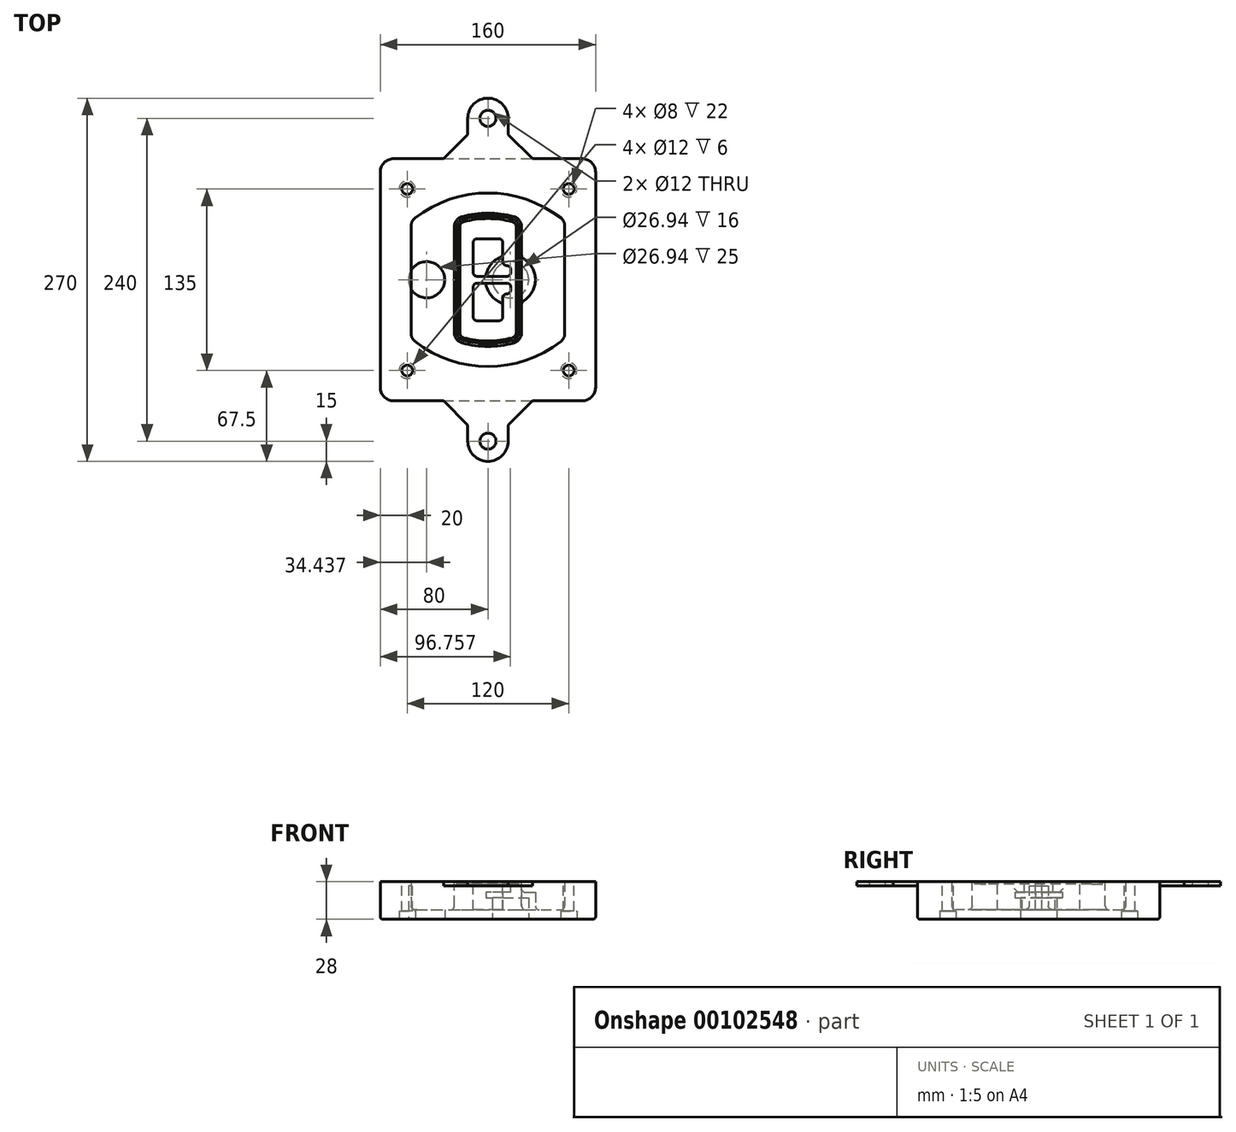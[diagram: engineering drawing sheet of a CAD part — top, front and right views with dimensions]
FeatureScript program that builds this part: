
annotation { "Feature Type Name" : "Feature", "Feature Type Description" : "" }
export const myFeature = defineFeature(function(context is Context, id is Id, definition is map)
    precondition{}
    {
        {
            var Q0;
            Q0=qCreatedBy(makeId("Top.planeOp"),FACE);
            var sketch = newSketch(context, id + "F0", { "sketchPlane" : qUnion([Q0])});
            skPoint(sketch, "E0.rect.middle", {"position": v(0, 0) * mm});
            skLineSegment(sketch, "E1.bottom", {"start": v(-70, -90) * mm, "end": v(70, -90) * mm});
            skLineSegment(sketch, "E1.top", {"start": v(-70, 90) * mm, "end": v(70, 90) * mm});
            skLineSegment(sketch, "E1.left", {"start": v(-80, -80) * mm, "end": v(-80, 80) * mm});
            skLineSegment(sketch, "E1.right", {"start": v(80, -80) * mm, "end": v(80, 80) * mm});
            skLineSegment(sketch, "E2", {"start": v(-80, 90) * mm, "end": v(80, -90) * mm, "construction": true});
            skLineSegment(sketch, "E3", {"start": v(80, 90) * mm, "end": v(-80, -90) * mm, "construction": true});
            skCircle(sketch, "E4", {"center": v(-60, 67.5) * mm, "radius": 4 * mm});
            skCircle(sketch, "E5", {"center": v(60, 67.5) * mm, "radius": 4 * mm});
            skCircle(sketch, "E6", {"center": v(60, -67.5) * mm, "radius": 4 * mm});
            skCircle(sketch, "E7", {"center": v(-60, -67.5) * mm, "radius": 4 * mm});
            skLineSegment(sketch, "E8", {"start": v(-60, 67.5) * mm, "end": v(60, 67.5) * mm, "construction": true});
            skLineSegment(sketch, "E9", {"start": v(60, 67.5) * mm, "end": v(60, -67.5) * mm, "construction": true});
            skLineSegment(sketch, "E10", {"start": v(60, -67.5) * mm, "end": v(-60, -67.5) * mm, "construction": true});
            skLineSegment(sketch, "E11", {"start": v(-60, -67.5) * mm, "end": v(-60, 67.5) * mm, "construction": true});
            skLineSegment(sketch, "E12", {"start": v(-60, 40.3) * mm, "end": v(-60, -40.3) * mm});
            skLineSegment(sketch, "E13", {"start": v(60, 40.3) * mm, "end": v(60, -40.3) * mm});
            skArc(sketch, "E14", {"start": v(56.15, 48.18) * mm, "mid": v(0, 67.5) * mm, "end": v(-56.15, 48.18) * mm});
            skArc(sketch, "E15", {"start": v(-56.15, -48.18) * mm, "mid": v(0, -67.5) * mm, "end": v(56.15, -48.18) * mm});
            skLineSegment(sketch, "E16", {"start": v(-60, 0) * mm, "end": v(60, 0) * mm, "construction": true});
            skPoint(sketch, "E17.visualSharp", {"position": v(-60, -45) * mm});
            skArc(sketch, "E17.filletArc", {"start": v(-60, -40.3) * mm, "mid": v(-58.99, -44.68) * mm, "end": v(-56.15, -48.18) * mm});
            skPoint(sketch, "E18.visualSharp", {"position": v(-60, 45) * mm});
            skArc(sketch, "E18.filletArc", {"start": v(-56.15, 48.18) * mm, "mid": v(-58.99, 44.68) * mm, "end": v(-60, 40.3) * mm});
            skPoint(sketch, "E19.visualSharp", {"position": v(60, 45) * mm});
            skArc(sketch, "E19.filletArc", {"start": v(60, 40.3) * mm, "mid": v(58.99, 44.68) * mm, "end": v(56.15, 48.18) * mm});
            skPoint(sketch, "E20.visualSharp", {"position": v(60, -45) * mm});
            skArc(sketch, "E20.filletArc", {"start": v(56.15, -48.18) * mm, "mid": v(58.99, -44.68) * mm, "end": v(60, -40.3) * mm});
            skPoint(sketch, "E21.visualSharp", {"position": v(-80, 90) * mm});
            skArc(sketch, "E21.filletArc", {"start": v(-70, 90) * mm, "mid": v(-77.07, 87.07) * mm, "end": v(-80, 80) * mm});
            skPoint(sketch, "E22.visualSharp", {"position": v(80, 90) * mm});
            skArc(sketch, "E22.filletArc", {"start": v(80, 80) * mm, "mid": v(77.07, 87.07) * mm, "end": v(70, 90) * mm});
            skPoint(sketch, "E23.visualSharp", {"position": v(80, -90) * mm});
            skArc(sketch, "E23.filletArc", {"start": v(70, -90) * mm, "mid": v(77.07, -87.07) * mm, "end": v(80, -80) * mm});
            skPoint(sketch, "E24.visualSharp", {"position": v(-80, -90) * mm});
            skArc(sketch, "E24.filletArc", {"start": v(-80, -80) * mm, "mid": v(-77.07, -87.07) * mm, "end": v(-70, -90) * mm});
            skArc(sketch, "E25.0", {"start": v(57, 40.3) * mm, "mid": v(56.3, 43.36) * mm, "end": v(54.3, 45.81) * mm});
            skLineSegment(sketch, "E25.1", {"start": v(57, 40.3) * mm, "end": v(57, -40.3) * mm});
            skArc(sketch, "E25.2", {"start": v(54.3, -45.81) * mm, "mid": v(56.3, -43.36) * mm, "end": v(57, -40.3) * mm});
            skArc(sketch, "E25.3", {"start": v(-54.3, -45.81) * mm, "mid": v(0, -64.5) * mm, "end": v(54.3, -45.81) * mm});
            skArc(sketch, "E25.4", {"start": v(-57, -40.3) * mm, "mid": v(-56.3, -43.36) * mm, "end": v(-54.3, -45.81) * mm});
            skArc(sketch, "E25.5", {"start": v(54.3, 45.81) * mm, "mid": v(0, 64.5) * mm, "end": v(-54.3, 45.81) * mm});
            skLineSegment(sketch, "E25.6", {"start": v(-57, 40.3) * mm, "end": v(-57, -40.3) * mm});
            skArc(sketch, "E25.7", {"start": v(-54.3, 45.81) * mm, "mid": v(-56.3, 43.36) * mm, "end": v(-57, 40.3) * mm});
            skArc(sketch, "E26.0", {"start": v(-58.62, 51.33) * mm, "mid": v(-62.58, 46.43) * mm, "end": v(-64, 40.3) * mm});
            skArc(sketch, "E26.1", {"start": v(58.62, 51.33) * mm, "mid": v(0, 71.5) * mm, "end": v(-58.62, 51.33) * mm});
            skArc(sketch, "E26.2", {"start": v(64, 40.3) * mm, "mid": v(62.58, 46.43) * mm, "end": v(58.62, 51.33) * mm});
            skLineSegment(sketch, "E26.3", {"start": v(64, 40.3) * mm, "end": v(64, -40.3) * mm});
            skArc(sketch, "E26.4", {"start": v(58.62, -51.33) * mm, "mid": v(62.58, -46.43) * mm, "end": v(64, -40.3) * mm});
            skLineSegment(sketch, "E26.5", {"start": v(-64, 40.3) * mm, "end": v(-64, -40.3) * mm});
            skArc(sketch, "E26.6", {"start": v(-58.62, -51.33) * mm, "mid": v(0, -71.5) * mm, "end": v(58.62, -51.33) * mm});
            skArc(sketch, "E26.7", {"start": v(-64, -40.3) * mm, "mid": v(-62.58, -46.43) * mm, "end": v(-58.62, -51.33) * mm});
            skSolve(sketch);
        }
        {
            var Q0;
            Q0=makeQuery(id+"F0.imprint","IMPRINT",FACE,{"disambiguationData":[TD([[makeQuery(id+"F0.imprint","IMPRINT",EDGE,{"derivedFrom":sQuery(id+"F0.wireOp",EDGE,"E1.bottom")}),1.0]])]});
            var Q1;
            Q1=makeQuery(id+"F0.imprint","IMPRINT",FACE,{"disambiguationData":[TD([[makeQuery(id+"F0.imprint","IMPRINT",EDGE,{"derivedFrom":sQuery(id+"F0.wireOp",EDGE,"E12")}),1.0]])]});
            var Q2;
            Q2=makeQuery(id+"F0.imprint","IMPRINT",FACE,{"disambiguationData":[TD([[makeQuery(id+"F0.imprint","IMPRINT",EDGE,{"derivedFrom":sQuery(id+"F0.wireOp",EDGE,"E25.0")}),1.0]])]});
            var Q3;
            Q3=makeQuery(id+"F0.imprint","IMPRINT",FACE,{"disambiguationData":[TD([[makeQuery(id+"F0.imprint","IMPRINT",EDGE,{"derivedFrom":sQuery(id+"F0.wireOp",EDGE,"E12")}),-1.0]])]});
            extrude(context, id + "F1", {"entities" : qUnion([Q0, Q1, Q2, Q3]), "oppositeDirection" : true, "depth" : 25 * mm});
        }
        {
            var Q0;
            Q0=makeQuery(id+"F0.imprint","IMPRINT",FACE,{"disambiguationData":[TD([[makeQuery(id+"F0.imprint","IMPRINT",EDGE,{"derivedFrom":sQuery(id+"F0.wireOp",EDGE,"E12")}),1.0]])]});
            extrude(context, id + "F2", {"entities" : qUnion([Q0]), "operationType" : NewBodyOperationType.ADD, "depth" : 3 * mm});
        }
        {
            var Q0;
            Q0=makeQuery(id+"F0.imprint","IMPRINT",FACE,{"disambiguationData":[TD([[makeQuery(id+"F0.imprint","IMPRINT",EDGE,{"derivedFrom":sQuery(id+"F0.wireOp",EDGE,"E25.0")}),1.0]])]});
            extrude(context, id + "F3", {"entities" : qUnion([Q0]), "operationType" : NewBodyOperationType.REMOVE, "oppositeDirection" : true, "depth" : 18 * mm});
        }
        {
            var Q0;
            Q0=makeQuery(id+"F2.opExtrude","CAP_FACE",FACE,{"disambiguationData":[OSD([sQuery(id+"F0.wireOp",EDGE,"E12"),sQuery(id+"F0.wireOp",EDGE,"E13"),sQuery(id+"F0.wireOp",EDGE,"E14"),sQuery(id+"F0.wireOp",EDGE,"E15"),sQuery(id+"F0.wireOp",EDGE,"E17.filletArc"),sQuery(id+"F0.wireOp",EDGE,"E18.filletArc"),sQuery(id+"F0.wireOp",EDGE,"E19.filletArc"),sQuery(id+"F0.wireOp",EDGE,"E20.filletArc"),sQuery(id+"F0.wireOp",EDGE,"E25.0"),sQuery(id+"F0.wireOp",EDGE,"E25.1"),sQuery(id+"F0.wireOp",EDGE,"E25.2"),sQuery(id+"F0.wireOp",EDGE,"E25.3"),sQuery(id+"F0.wireOp",EDGE,"E25.4"),sQuery(id+"F0.wireOp",EDGE,"E25.5"),sQuery(id+"F0.wireOp",EDGE,"E25.6"),sQuery(id+"F0.wireOp",EDGE,"E25.7")])],"isStart":false});
            var sketch = newSketch(context, id + "F4", { "sketchPlane" : qUnion([Q0])});
            skArc(sketch, "E27.0", {"start": v(-19.08, -46.97) * mm, "mid": v(0, -49.5) * mm, "end": v(19.08, -46.97) * mm});
            skArc(sketch, "E28.0", {"start": v(19.08, 46.97) * mm, "mid": v(0, 49.5) * mm, "end": v(-19.08, 46.97) * mm});
            skLineSegment(sketch, "E29", {"start": v(-25, 39.25) * mm, "end": v(-25, -39.25) * mm});
            skLineSegment(sketch, "E30", {"start": v(25, 39.25) * mm, "end": v(25, -39.25) * mm});
            skLineSegment(sketch, "E31", {"start": v(-25, 45.1) * mm, "end": v(25, 45.1) * mm, "construction": true});
            skLineSegment(sketch, "E32", {"start": v(-25, -45.1) * mm, "end": v(25, -45.1) * mm, "construction": true});
            skPoint(sketch, "E33.visualSharp", {"position": v(-25, 45.1) * mm});
            skArc(sketch, "E33.filletArc", {"start": v(-19.08, 46.97) * mm, "mid": v(-23.35, 44.11) * mm, "end": v(-25, 39.25) * mm});
            skPoint(sketch, "E34.visualSharp", {"position": v(25, 45.1) * mm});
            skArc(sketch, "E34.filletArc", {"start": v(25, 39.25) * mm, "mid": v(23.35, 44.11) * mm, "end": v(19.08, 46.97) * mm});
            skPoint(sketch, "E35.visualSharp", {"position": v(25, -45.1) * mm});
            skArc(sketch, "E35.filletArc", {"start": v(19.08, -46.97) * mm, "mid": v(23.35, -44.11) * mm, "end": v(25, -39.25) * mm});
            skPoint(sketch, "E36.visualSharp", {"position": v(-25, -45.1) * mm});
            skArc(sketch, "E36.filletArc", {"start": v(-25, -39.25) * mm, "mid": v(-23.35, -44.11) * mm, "end": v(-19.08, -46.97) * mm});
            skArc(sketch, "E37.0", {"start": v(54.3, 45.81) * mm, "mid": v(0, 64.5) * mm, "end": v(-54.3, 45.81) * mm});
            skArc(sketch, "E37.1", {"start": v(-54.3, 45.81) * mm, "mid": v(-56.3, 43.36) * mm, "end": v(-57, 40.3) * mm});
            skLineSegment(sketch, "E37.2", {"start": v(-57, 40.3) * mm, "end": v(-57, -40.3) * mm});
            skArc(sketch, "E37.3", {"start": v(-57, -40.3) * mm, "mid": v(-56.3, -43.36) * mm, "end": v(-54.3, -45.81) * mm});
            skArc(sketch, "E37.4", {"start": v(-54.3, -45.81) * mm, "mid": v(0, -64.5) * mm, "end": v(54.3, -45.81) * mm});
            skArc(sketch, "E37.5", {"start": v(54.3, -45.81) * mm, "mid": v(56.3, -43.36) * mm, "end": v(57, -40.3) * mm});
            skLineSegment(sketch, "E37.6", {"start": v(57, 40.3) * mm, "end": v(57, -40.3) * mm});
            skArc(sketch, "E37.7", {"start": v(57, 40.3) * mm, "mid": v(56.3, 43.36) * mm, "end": v(54.3, 45.81) * mm});
            skLineSegment(sketch, "E38.0", {"start": v(23, 39.25) * mm, "end": v(23, -39.25) * mm});
            skArc(sketch, "E38.1", {"start": v(18.56, -45.04) * mm, "mid": v(21.76, -42.9) * mm, "end": v(23, -39.25) * mm});
            skArc(sketch, "E38.2", {"start": v(-18.56, -45.04) * mm, "mid": v(0, -47.5) * mm, "end": v(18.56, -45.04) * mm});
            skArc(sketch, "E38.3", {"start": v(-23, -39.25) * mm, "mid": v(-21.76, -42.9) * mm, "end": v(-18.56, -45.04) * mm});
            skLineSegment(sketch, "E38.4", {"start": v(-23, 39.25) * mm, "end": v(-23, -39.25) * mm});
            skArc(sketch, "E38.5", {"start": v(23, 39.25) * mm, "mid": v(21.76, 42.9) * mm, "end": v(18.56, 45.04) * mm});
            skArc(sketch, "E38.6", {"start": v(-18.56, 45.04) * mm, "mid": v(-21.76, 42.9) * mm, "end": v(-23, 39.25) * mm});
            skArc(sketch, "E38.7", {"start": v(18.56, 45.04) * mm, "mid": v(0, 47.5) * mm, "end": v(-18.56, 45.04) * mm});
            skArc(sketch, "E39.0", {"start": v(21, 39.25) * mm, "mid": v(20.18, 41.68) * mm, "end": v(18.04, 43.1) * mm});
            skLineSegment(sketch, "E39.1", {"start": v(21, 39.25) * mm, "end": v(21, -39.25) * mm});
            skArc(sketch, "E39.2", {"start": v(18.04, -43.1) * mm, "mid": v(20.18, -41.68) * mm, "end": v(21, -39.25) * mm});
            skArc(sketch, "E39.3", {"start": v(-18.04, -43.1) * mm, "mid": v(0, -45.5) * mm, "end": v(18.04, -43.1) * mm});
            skArc(sketch, "E39.4", {"start": v(-21, -39.25) * mm, "mid": v(-20.18, -41.68) * mm, "end": v(-18.04, -43.1) * mm});
            skArc(sketch, "E39.5", {"start": v(18.04, 43.1) * mm, "mid": v(0, 45.5) * mm, "end": v(-18.04, 43.1) * mm});
            skLineSegment(sketch, "E39.6", {"start": v(-21, 39.25) * mm, "end": v(-21, -39.25) * mm});
            skArc(sketch, "E39.7", {"start": v(-18.04, 43.1) * mm, "mid": v(-20.18, 41.68) * mm, "end": v(-21, 39.25) * mm});
            skLineSegment(sketch, "E40", {"start": v(-25, 0) * mm, "end": v(25, 0) * mm, "construction": true});
            skLineSegment(sketch, "E41", {"start": v(-11, 5.5) * mm, "end": v(-11, 27.5) * mm});
            skLineSegment(sketch, "E42", {"start": v(-8, 30.5) * mm, "end": v(8, 30.5) * mm});
            skLineSegment(sketch, "E43", {"start": v(11, 27.5) * mm, "end": v(11, 13.5) * mm});
            skLineSegment(sketch, "E44", {"start": v(14, 10.5) * mm, "end": v(14, 10.5) * mm});
            skLineSegment(sketch, "E45", {"start": v(17, 7.5) * mm, "end": v(17, 5.5) * mm});
            skLineSegment(sketch, "E46", {"start": v(14, 2.5) * mm, "end": v(-8, 2.5) * mm});
            skPoint(sketch, "E47.visualSharp", {"position": v(-11, 30.5) * mm});
            skArc(sketch, "E47.filletArc", {"start": v(-8, 30.5) * mm, "mid": v(-10.12, 29.62) * mm, "end": v(-11, 27.5) * mm});
            skPoint(sketch, "E48.visualSharp", {"position": v(11, 30.5) * mm});
            skArc(sketch, "E48.filletArc", {"start": v(11, 27.5) * mm, "mid": v(10.12, 29.62) * mm, "end": v(8, 30.5) * mm});
            skPoint(sketch, "E49.visualSharp", {"position": v(11, 10.5) * mm});
            skArc(sketch, "E49.filletArc", {"start": v(11, 13.5) * mm, "mid": v(11.88, 11.38) * mm, "end": v(14, 10.5) * mm});
            skPoint(sketch, "E50.visualSharp", {"position": v(17, 10.5) * mm});
            skArc(sketch, "E50.filletArc", {"start": v(17, 7.5) * mm, "mid": v(16.12, 9.62) * mm, "end": v(14, 10.5) * mm});
            skPoint(sketch, "E51.visualSharp", {"position": v(17, 2.5) * mm});
            skArc(sketch, "E51.filletArc", {"start": v(14, 2.5) * mm, "mid": v(16.12, 3.38) * mm, "end": v(17, 5.5) * mm});
            skPoint(sketch, "E52.visualSharp", {"position": v(-11, 2.5) * mm});
            skArc(sketch, "E52.filletArc", {"start": v(-11, 5.5) * mm, "mid": v(-10.12, 3.38) * mm, "end": v(-8, 2.5) * mm});
            skLineSegment(sketch, "E53.0.MirrorCS", {"start": v(14, -2.5) * mm, "end": v(-8, -2.5) * mm});
            skArc(sketch, "E54.0.MirrorCS", {"start": v(-11, -5.5) * mm, "mid": v(-10.12, -3.38) * mm, "end": v(-8, -2.5) * mm});
            skLineSegment(sketch, "E55.0.MirrorCS", {"start": v(-11, -5.5) * mm, "end": v(-11, -27.5) * mm});
            skArc(sketch, "E56.0.MirrorCS", {"start": v(-8, -30.5) * mm, "mid": v(-10.12, -29.62) * mm, "end": v(-11, -27.5) * mm});
            skLineSegment(sketch, "E57.0.MirrorCS", {"start": v(-8, -30.5) * mm, "end": v(8, -30.5) * mm});
            skArc(sketch, "E58.0.MirrorCS", {"start": v(11, -27.5) * mm, "mid": v(10.12, -29.62) * mm, "end": v(8, -30.5) * mm});
            skLineSegment(sketch, "E59.0.MirrorCS", {"start": v(11, -27.5) * mm, "end": v(11, -13.5) * mm});
            skArc(sketch, "E60.0.MirrorCS", {"start": v(11, -13.5) * mm, "mid": v(11.88, -11.38) * mm, "end": v(14, -10.5) * mm});
            skArc(sketch, "E61.0.MirrorCS", {"start": v(17, -7.5) * mm, "mid": v(16.12, -9.62) * mm, "end": v(14, -10.5) * mm});
            skLineSegment(sketch, "E62.0.MirrorCS", {"start": v(17, -7.5) * mm, "end": v(17, -5.5) * mm});
            skArc(sketch, "E63.0.MirrorCS", {"start": v(14, -2.5) * mm, "mid": v(16.12, -3.38) * mm, "end": v(17, -5.5) * mm});
            skSolve(sketch);
        }
        {
            var Q0;
            Q0=makeQuery(id+"F4.imprint","IMPRINT",FACE,{"disambiguationData":[TD([[makeQuery(id+"F4.imprint","IMPRINT",EDGE,{"derivedFrom":sQuery(id+"F4.wireOp",EDGE,"E27.0")}),1.0]])]});
            var Q1;
            Q1=makeQuery(id+"F4.imprint","IMPRINT",FACE,{"disambiguationData":[TD([[makeQuery(id+"F4.imprint","IMPRINT",EDGE,{"derivedFrom":sQuery(id+"F4.wireOp",EDGE,"E38.0")}),-1.0]])]});
            var Q2;
            Q2=makeQuery(id+"F4.imprint","IMPRINT",FACE,{"disambiguationData":[TD([[makeQuery(id+"F4.imprint","IMPRINT",EDGE,{"derivedFrom":sQuery(id+"F4.wireOp",EDGE,"E39.0")}),1.0]])]});
            extrude(context, id + "F5", {"entities" : qUnion([Q0, Q1, Q2]), "operationType" : NewBodyOperationType.ADD, "endBound" : BoundingType.UP_TO_NEXT, "oppositeDirection" : true, "depth" : 25 * mm});
        }
        {
            var Q0;
            Q0=makeQuery(id+"F4.imprint","IMPRINT",FACE,{"disambiguationData":[TD([[makeQuery(id+"F4.imprint","IMPRINT",EDGE,{"derivedFrom":sQuery(id+"F4.wireOp",EDGE,"E38.0")}),-1.0]])]});
            extrude(context, id + "F6", {"entities" : qUnion([Q0]), "operationType" : NewBodyOperationType.REMOVE, "oppositeDirection" : true, "depth" : 2 * mm});
        }
        {
            var Q0;
            Q0=makeQuery(id+"F1.opExtrude","CAP_FACE",FACE,{"disambiguationData":[OSD([sQuery(id+"F0.wireOp",EDGE,"E1.bottom"),sQuery(id+"F0.wireOp",EDGE,"E1.top"),sQuery(id+"F0.wireOp",EDGE,"E1.left"),sQuery(id+"F0.wireOp",EDGE,"E1.right"),sQuery(id+"F0.wireOp",EDGE,"E4"),sQuery(id+"F0.wireOp",EDGE,"E5"),sQuery(id+"F0.wireOp",EDGE,"E6"),sQuery(id+"F0.wireOp",EDGE,"E7"),sQuery(id+"F0.wireOp",EDGE,"E21.filletArc"),sQuery(id+"F0.wireOp",EDGE,"E22.filletArc"),sQuery(id+"F0.wireOp",EDGE,"E23.filletArc"),sQuery(id+"F0.wireOp",EDGE,"E24.filletArc")])],"isStart":false});
            var sketch = newSketch(context, id + "F7", { "sketchPlane" : qUnion([Q0])});
            skCircle(sketch, "E64", {"center": v(16.76, 0) * mm, "radius": 13.47 * mm});
            skCircle(sketch, "E65", {"center": v(-45.56, 0) * mm, "radius": 13.47 * mm});
            skLineSegment(sketch, "E66", {"start": v(80, 0) * mm, "end": v(-80, 0) * mm});
            skCircle(sketch, "E67", {"center": v(16.76, 0) * mm, "radius": 18.47 * mm});
            skCircle(sketch, "E68", {"center": v(60, -67.5) * mm, "radius": 6 * mm});
            skCircle(sketch, "E69", {"center": v(-60, -67.5) * mm, "radius": 6 * mm});
            skCircle(sketch, "E70", {"center": v(-60, 67.5) * mm, "radius": 6 * mm});
            skCircle(sketch, "E71", {"center": v(60, 67.5) * mm, "radius": 6 * mm});
            skSolve(sketch);
        }
        {
            var Q0;
            {var subQ1=sQuery(id+"F7.wireOp",EDGE,"E66");var subQ4=sQuery(id+"F7.wireOp",EDGE,"E64");var subQ6=makeQuery(id+"F7.imprint","INTERSECT",VERTEX,{"disambiguationData":[OD(0.0)],"derivedFrom":[subQ4,subQ1]});Q0=makeQuery(id+"F7.imprint","IMPRINT",FACE,{"disambiguationData":[TD([[makeQuery(id+"F7.imprint","IMPRINT",EDGE,{"disambiguationData":[TD([[subQ6,-1.0]])],"derivedFrom":subQ4}),-1.0]])]});}
            var Q1;
            {var subQ0=sQuery(id+"F7.wireOp",EDGE,"E66");var subQ1=sQuery(id+"F7.wireOp",EDGE,"E64");var subQ3=makeQuery(id+"F7.imprint","INTERSECT",VERTEX,{"disambiguationData":[OD(0.0)],"derivedFrom":[subQ1,subQ0]});Q1=makeQuery(id+"F7.imprint","IMPRINT",FACE,{"disambiguationData":[TD([[makeQuery(id+"F7.imprint","IMPRINT",EDGE,{"disambiguationData":[TD([[subQ3,-1.0]])],"derivedFrom":subQ1}),1.0]])]});}
            var Q2;
            {var subQ0=sQuery(id+"F7.wireOp",EDGE,"E66");var subQ1=sQuery(id+"F7.wireOp",EDGE,"E64");var subQ3=makeQuery(id+"F7.imprint","INTERSECT",VERTEX,{"disambiguationData":[OD(0.0)],"derivedFrom":[subQ1,subQ0]});Q2=makeQuery(id+"F7.imprint","IMPRINT",FACE,{"disambiguationData":[TD([[makeQuery(id+"F7.imprint","IMPRINT",EDGE,{"disambiguationData":[TD([[subQ3,1.0]])],"derivedFrom":subQ1}),1.0]])]});}
            var Q3;
            {var subQ1=sQuery(id+"F7.wireOp",EDGE,"E66");var subQ4=sQuery(id+"F7.wireOp",EDGE,"E64");var subQ6=makeQuery(id+"F7.imprint","INTERSECT",VERTEX,{"disambiguationData":[OD(0.0)],"derivedFrom":[subQ4,subQ1]});Q3=makeQuery(id+"F7.imprint","IMPRINT",FACE,{"disambiguationData":[TD([[makeQuery(id+"F7.imprint","IMPRINT",EDGE,{"disambiguationData":[TD([[subQ6,1.0]])],"derivedFrom":subQ4}),-1.0]])]});}
            extrude(context, id + "F8", {"entities" : qUnion([Q0, Q1, Q2, Q3]), "operationType" : NewBodyOperationType.ADD, "oppositeDirection" : true, "depth" : 20 * mm});
        }
        {
            var Q0;
            {var subQ0=sQuery(id+"F7.wireOp",EDGE,"E66");var subQ1=sQuery(id+"F7.wireOp",EDGE,"E64");var subQ3=makeQuery(id+"F7.imprint","INTERSECT",VERTEX,{"disambiguationData":[OD(0.0)],"derivedFrom":[subQ1,subQ0]});Q0=makeQuery(id+"F7.imprint","IMPRINT",FACE,{"disambiguationData":[TD([[makeQuery(id+"F7.imprint","IMPRINT",EDGE,{"disambiguationData":[TD([[subQ3,-1.0]])],"derivedFrom":subQ1}),1.0]])]});}
            var Q1;
            {var subQ0=sQuery(id+"F7.wireOp",EDGE,"E66");var subQ1=sQuery(id+"F7.wireOp",EDGE,"E64");var subQ3=makeQuery(id+"F7.imprint","INTERSECT",VERTEX,{"disambiguationData":[OD(0.0)],"derivedFrom":[subQ1,subQ0]});Q1=makeQuery(id+"F7.imprint","IMPRINT",FACE,{"disambiguationData":[TD([[makeQuery(id+"F7.imprint","IMPRINT",EDGE,{"disambiguationData":[TD([[subQ3,1.0]])],"derivedFrom":subQ1}),1.0]])]});}
            extrude(context, id + "F9", {"entities" : qUnion([Q0, Q1]), "operationType" : NewBodyOperationType.REMOVE, "oppositeDirection" : true, "depth" : 16 * mm});
        }
        {
            var Q0;
            {var subQ0=sQuery(id+"F7.wireOp",EDGE,"E66");var subQ1=sQuery(id+"F7.wireOp",EDGE,"E65");var subQ3=makeQuery(id+"F7.imprint","INTERSECT",VERTEX,{"disambiguationData":[OD(0.0)],"derivedFrom":[subQ1,subQ0]});Q0=makeQuery(id+"F7.imprint","IMPRINT",FACE,{"disambiguationData":[TD([[makeQuery(id+"F7.imprint","IMPRINT",EDGE,{"disambiguationData":[TD([[subQ3,-1.0]])],"derivedFrom":subQ1}),1.0]])]});}
            var Q1;
            {var subQ0=sQuery(id+"F7.wireOp",EDGE,"E66");var subQ1=sQuery(id+"F7.wireOp",EDGE,"E65");var subQ3=makeQuery(id+"F7.imprint","INTERSECT",VERTEX,{"disambiguationData":[OD(0.0)],"derivedFrom":[subQ1,subQ0]});Q1=makeQuery(id+"F7.imprint","IMPRINT",FACE,{"disambiguationData":[TD([[makeQuery(id+"F7.imprint","IMPRINT",EDGE,{"disambiguationData":[TD([[subQ3,1.0]])],"derivedFrom":subQ1}),1.0]])]});}
            extrude(context, id + "F10", {"entities" : qUnion([Q0, Q1]), "operationType" : NewBodyOperationType.REMOVE, "oppositeDirection" : true, "depth" : 25 * mm});
        }
        {
            var Q0;
            Q0=makeQuery(id+"F7.imprint","IMPRINT",FACE,{"disambiguationData":[TD([[makeQuery(id+"F7.imprint","IMPRINT",EDGE,{"derivedFrom":sQuery(id+"F7.wireOp",EDGE,"E68")}),1.0]])]});
            var Q1;
            Q1=makeQuery(id+"F7.imprint","IMPRINT",FACE,{"disambiguationData":[TD([[makeQuery(id+"F7.imprint","IMPRINT",EDGE,{"derivedFrom":makeQuery(id+"F1.opExtrude","CAP_EDGE",EDGE,{"disambiguationData":[OSD([sQuery(id+"F0.wireOp",EDGE,"E5")])],"isStart":false})}),-1.0]])]});
            var Q2;
            Q2=makeQuery(id+"F7.imprint","IMPRINT",FACE,{"disambiguationData":[TD([[makeQuery(id+"F7.imprint","IMPRINT",EDGE,{"derivedFrom":sQuery(id+"F7.wireOp",EDGE,"E69")}),1.0]])]});
            var Q3;
            Q3=makeQuery(id+"F7.imprint","IMPRINT",FACE,{"disambiguationData":[TD([[makeQuery(id+"F7.imprint","IMPRINT",EDGE,{"derivedFrom":makeQuery(id+"F1.opExtrude","CAP_EDGE",EDGE,{"disambiguationData":[OSD([sQuery(id+"F0.wireOp",EDGE,"E4")])],"isStart":false})}),-1.0]])]});
            var Q4;
            Q4=makeQuery(id+"F7.imprint","IMPRINT",FACE,{"disambiguationData":[TD([[makeQuery(id+"F7.imprint","IMPRINT",EDGE,{"derivedFrom":sQuery(id+"F7.wireOp",EDGE,"E70")}),1.0]])]});
            var Q5;
            Q5=makeQuery(id+"F7.imprint","IMPRINT",FACE,{"disambiguationData":[TD([[makeQuery(id+"F7.imprint","IMPRINT",EDGE,{"derivedFrom":makeQuery(id+"F1.opExtrude","CAP_EDGE",EDGE,{"disambiguationData":[OSD([sQuery(id+"F0.wireOp",EDGE,"E7")])],"isStart":false})}),-1.0]])]});
            var Q6;
            Q6=makeQuery(id+"F7.imprint","IMPRINT",FACE,{"disambiguationData":[TD([[makeQuery(id+"F7.imprint","IMPRINT",EDGE,{"derivedFrom":sQuery(id+"F7.wireOp",EDGE,"E71")}),1.0]])]});
            var Q7;
            Q7=makeQuery(id+"F7.imprint","IMPRINT",FACE,{"disambiguationData":[TD([[makeQuery(id+"F7.imprint","IMPRINT",EDGE,{"derivedFrom":makeQuery(id+"F1.opExtrude","CAP_EDGE",EDGE,{"disambiguationData":[OSD([sQuery(id+"F0.wireOp",EDGE,"E6")])],"isStart":false})}),-1.0]])]});
            extrude(context, id + "F11", {"entities" : qUnion([Q0, Q1, Q2, Q3, Q4, Q5, Q6, Q7]), "operationType" : NewBodyOperationType.REMOVE, "oppositeDirection" : true, "depth" : 6 * mm});
        }
        {
            var Q0;
            Q0=makeQuery(id+"F9.boolean.opBoolean","COPY",FACE,{"derivedFrom":makeQuery(id+"F9.opExtrude","CAP_FACE",FACE,{"disambiguationData":[OSD([sQuery(id+"F7.wireOp",EDGE,"E64")])],"isStart":false})});
            var sketch = newSketch(context, id + "F12", { "sketchPlane" : qUnion([Q0])});
            skArc(sketch, "E72.0", {"start": v(11, 17.55) * mm, "mid": v(2.57, 11.82) * mm, "end": v(-1.54, 2.5) * mm});
            skArc(sketch, "E72.1", {"start": v(-1.54, -2.5) * mm, "mid": v(2.57, -11.82) * mm, "end": v(11, -17.55) * mm});
            skLineSegment(sketch, "E73", {"start": v(-1.54, -2.5) * mm, "end": v(14, -2.5) * mm});
            skLineSegment(sketch, "E74.0", {"start": v(14, 2.5) * mm, "end": v(-1.54, 2.5) * mm});
            skArc(sketch, "E74.1", {"start": v(14, 2.5) * mm, "mid": v(16.12, 3.38) * mm, "end": v(17, 5.5) * mm});
            skLineSegment(sketch, "E74.2", {"start": v(17, 7.5) * mm, "end": v(17, 5.5) * mm});
            skArc(sketch, "E74.3", {"start": v(17, 7.5) * mm, "mid": v(16.12, 9.62) * mm, "end": v(14, 10.5) * mm});
            skArc(sketch, "E74.4", {"start": v(11, 13.5) * mm, "mid": v(11.88, 11.38) * mm, "end": v(14, 10.5) * mm});
            skLineSegment(sketch, "E74.5", {"start": v(11, 17.55) * mm, "end": v(11, 13.5) * mm});
            skLineSegment(sketch, "E74.7", {"start": v(14, -2.5) * mm, "end": v(-1.54, -2.5) * mm});
            skArc(sketch, "E74.8", {"start": v(14, -2.5) * mm, "mid": v(16.12, -3.38) * mm, "end": v(17, -5.5) * mm});
            skLineSegment(sketch, "E74.9", {"start": v(17, -7.5) * mm, "end": v(17, -5.5) * mm});
            skArc(sketch, "E74.10", {"start": v(17, -7.5) * mm, "mid": v(16.12, -9.62) * mm, "end": v(14, -10.5) * mm});
            skArc(sketch, "E74.11", {"start": v(11, -13.5) * mm, "mid": v(11.88, -11.38) * mm, "end": v(14, -10.5) * mm});
            skLineSegment(sketch, "E74.12", {"start": v(11, -17.55) * mm, "end": v(11, -13.5) * mm});
            skPoint(sketch, "E75.orphan", {"position": v(11, -27.5) * mm});
            skPoint(sketch, "E76.orphan", {"position": v(-8, -2.5) * mm});
            skPoint(sketch, "E77.orphan", {"position": v(-8, 2.5) * mm});
            skPoint(sketch, "E78.orphan", {"position": v(11, 27.5) * mm});
            skSolve(sketch);
        }
        {
            var Q0;
            {var subQ7=sQuery(id+"F12.wireOp",EDGE,"E72.0");var subQ14=sQuery(id+"F12.wireOp",EDGE,"E72.1");var subQ16=sQuery(id+"F12.wireOp",EDGE,"E74.1");var subQ18=sQuery(id+"F12.wireOp",EDGE,"E74.8");Q0=qUnion([makeQuery(id+"F12.imprint","IMPRINT",FACE,{"disambiguationData":[TD([[makeQuery(id+"F12.imprint","IMPRINT",EDGE,{"derivedFrom":subQ7}),1.0]])]}),makeQuery(id+"F12.imprint","IMPRINT",FACE,{"disambiguationData":[TD([[makeQuery(id+"F12.imprint","IMPRINT",EDGE,{"derivedFrom":subQ14}),1.0]])]}),makeQuery(id+"F12.imprint","IMPRINT",FACE,{"disambiguationData":[TD([[makeQuery(id+"F12.imprint","IMPRINT",EDGE,{"derivedFrom":subQ16}),1.0]])]}),makeQuery(id+"F12.imprint","IMPRINT",FACE,{"disambiguationData":[TD([[makeQuery(id+"F12.imprint","IMPRINT",EDGE,{"derivedFrom":subQ18}),-1.0]])]})]);}
            var Q1;
            Q1=makeQuery(id+"F5.boolean.opBoolean","SPLIT",FACE,{"disambiguationData":[TD([makeQuery(id+"F5.opExtrude","SWEPT_FACE",FACE,{"disambiguationData":[OSD([sQuery(id+"F4.wireOp",EDGE,"E41")])]})])],"derivedFrom":makeQuery(id+"F3.boolean.opBoolean","COPY",FACE,{"derivedFrom":makeQuery(id+"F3.opExtrude","CAP_FACE",FACE,{"disambiguationData":[OSD([sQuery(id+"F0.wireOp",EDGE,"E25.0"),sQuery(id+"F0.wireOp",EDGE,"E25.1"),sQuery(id+"F0.wireOp",EDGE,"E25.2"),sQuery(id+"F0.wireOp",EDGE,"E25.3"),sQuery(id+"F0.wireOp",EDGE,"E25.4"),sQuery(id+"F0.wireOp",EDGE,"E25.5"),sQuery(id+"F0.wireOp",EDGE,"E25.6"),sQuery(id+"F0.wireOp",EDGE,"E25.7")])],"isStart":false})})});
            extrude(context, id + "F13", {"entities" : qUnion([Q0]), "operationType" : NewBodyOperationType.REMOVE, "endBound" : BoundingType.UP_TO_SURFACE, "endBoundEntityFace" : qUnion([Q1]), "depth" : 25 * mm});
        }
        {
            var Q0;
            Q0=makeQuery(id+"F3.boolean.opBoolean","COPY",EDGE,{"derivedFrom":makeQuery(id+"F3.opExtrude","CAP_EDGE",EDGE,{"disambiguationData":[OSD([sQuery(id+"F0.wireOp",EDGE,"E25.6")])],"isStart":false})});
            var Q1;
            Q1=makeQuery(id+"F8.boolean.opBoolean","INTERSECT",EDGE,{"derivedFrom":[makeQuery(id+"F5.opExtrude","SWEPT_FACE",FACE,{"disambiguationData":[OSD([sQuery(id+"F4.wireOp",EDGE,"E30")])]}),makeQuery(id+"F8.opExtrude","CAP_FACE",FACE,{"disambiguationData":[OSD([sQuery(id+"F7.wireOp",EDGE,"E67")])],"isStart":false})]});
            var Q2;
            Q2=makeQuery(id+"F8.boolean.opBoolean","INTERSECT",EDGE,{"disambiguationData":[OD(1.0)],"derivedFrom":[makeQuery(id+"F5.opExtrude","SWEPT_FACE",FACE,{"disambiguationData":[OSD([sQuery(id+"F4.wireOp",EDGE,"E30")])]}),makeQuery(id+"F8.opExtrude","SWEPT_FACE",FACE,{"disambiguationData":[OSD([sQuery(id+"F7.wireOp",EDGE,"E67")])]})]});
            var Q3;
            {var subQ0=sQuery(id+"F4.wireOp",EDGE,"E30");Q3=makeQuery(id+"F8.boolean.opBoolean","SPLIT",EDGE,{"disambiguationData":[TD([makeQuery(id+"F5.opExtrude","SWEPT_FACE",FACE,{"disambiguationData":[OSD([sQuery(id+"F4.wireOp",EDGE,"E35.filletArc")])]})])],"derivedFrom":makeQuery(id+"F5.opExtrude","CAP_EDGE",EDGE,{"disambiguationData":[OSD([subQ0])],"isStart":false})});}
            var Q4;
            {var subQ0=sQuery(id+"F0.wireOp",EDGE,"E25.7");var subQ1=sQuery(id+"F0.wireOp",EDGE,"E25.1");var subQ2=sQuery(id+"F0.wireOp",EDGE,"E25.6");var subQ3=sQuery(id+"F0.wireOp",EDGE,"E25.5");var subQ4=sQuery(id+"F0.wireOp",EDGE,"E25.4");var subQ5=sQuery(id+"F0.wireOp",EDGE,"E25.0");var subQ6=sQuery(id+"F0.wireOp",EDGE,"E25.2");var subQ7=sQuery(id+"F0.wireOp",EDGE,"E25.3");Q4=makeQuery(id+"F8.boolean.opBoolean","INTERSECT",EDGE,{"derivedFrom":[makeQuery(id+"F5.boolean.opBoolean","SPLIT",FACE,{"disambiguationData":[TD([makeQuery(id+"F2.opExtrude","SWEPT_FACE",FACE,{"disambiguationData":[OSD([subQ5])]})])],"derivedFrom":makeQuery(id+"F3.boolean.opBoolean","COPY",FACE,{"derivedFrom":makeQuery(id+"F3.opExtrude","CAP_FACE",FACE,{"disambiguationData":[OSD([subQ5,subQ1,subQ6,subQ7,subQ4,subQ3,subQ2,subQ0])],"isStart":false})})}),makeQuery(id+"F8.opExtrude","SWEPT_FACE",FACE,{"disambiguationData":[OSD([sQuery(id+"F7.wireOp",EDGE,"E67")])]})]});}
            var Q5;
            Q5=makeQuery(id+"F8.boolean.opBoolean","INTERSECT",EDGE,{"disambiguationData":[OD(0.0)],"derivedFrom":[makeQuery(id+"F5.opExtrude","SWEPT_FACE",FACE,{"disambiguationData":[OSD([sQuery(id+"F4.wireOp",EDGE,"E30")])]}),makeQuery(id+"F8.opExtrude","SWEPT_FACE",FACE,{"disambiguationData":[OSD([sQuery(id+"F7.wireOp",EDGE,"E67")])]})]});
            fillet(context, id + "F14", {"entities" : qUnion([Q0, Q1, Q2, Q3, Q4, Q5]), "radius" : 3 * mm, "tangentPropagation" : true, "allowEdgeOverflow" : false});
        }
        {
            var Q0;
            Q0=makeQuery(id+"F1.opExtrude","CAP_EDGE",EDGE,{"disambiguationData":[OSD([sQuery(id+"F0.wireOp",EDGE,"E1.bottom")])],"isStart":false});
            fillet(context, id + "F15", {"entities" : qUnion([Q0]), "radius" : 2 * mm, "tangentPropagation" : true, "allowEdgeOverflow" : false});
        }
        {
            var Q0;
            {var subQ0=sQuery(id+"F0.wireOp",EDGE,"E22.filletArc");var subQ1=sQuery(id+"F0.wireOp",EDGE,"E7");var subQ2=sQuery(id+"F0.wireOp",EDGE,"E6");var subQ3=sQuery(id+"F0.wireOp",EDGE,"E5");var subQ4=sQuery(id+"F0.wireOp",EDGE,"E4");var subQ5=sQuery(id+"F0.wireOp",EDGE,"E1.bottom");var subQ6=sQuery(id+"F0.wireOp",EDGE,"E21.filletArc");var subQ7=sQuery(id+"F0.wireOp",EDGE,"E1.top");var subQ8=sQuery(id+"F0.wireOp",EDGE,"E1.left");var subQ9=sQuery(id+"F0.wireOp",EDGE,"E1.right");var subQ10=sQuery(id+"F0.wireOp",EDGE,"E23.filletArc");var subQ11=sQuery(id+"F0.wireOp",EDGE,"E24.filletArc");Q0=makeQuery(id+"F2.boolean.opBoolean","SPLIT",FACE,{"disambiguationData":[TD([makeQuery(id+"F1.opExtrude","SWEPT_FACE",FACE,{"disambiguationData":[OSD([subQ5])]})])],"derivedFrom":makeQuery(id+"F1.opExtrude","CAP_FACE",FACE,{"disambiguationData":[OSD([subQ5,subQ7,subQ8,subQ9,subQ4,subQ3,subQ2,subQ1,subQ6,subQ0,subQ10,subQ11])],"isStart":true})});}
            var sketch = newSketch(context, id + "F16", { "sketchPlane" : qUnion([Q0])});
            skLineSegment(sketch, "E79", {"start": v(0, 90) * mm, "end": v(0, 120) * mm, "construction": true});
            skCircle(sketch, "E80", {"center": v(0, 120) * mm, "radius": 6 * mm});
            skLineSegment(sketch, "E81", {"start": v(-33, 90) * mm, "end": v(-15, 108) * mm});
            skLineSegment(sketch, "E82", {"start": v(-15, 108) * mm, "end": v(-15, 120) * mm});
            skArc(sketch, "E83", {"start": v(15, 120) * mm, "mid": v(0, 135) * mm, "end": v(-15, 120) * mm});
            skLineSegment(sketch, "E84", {"start": v(15, 120) * mm, "end": v(15, 108) * mm});
            skLineSegment(sketch, "E85", {"start": v(15, 108) * mm, "end": v(33, 90) * mm});
            skLineSegment(sketch, "E86", {"start": v(-80, 0) * mm, "end": v(80, 0) * mm, "construction": true});
            skLineSegment(sketch, "E87.MirrorCS", {"start": v(-33, -90) * mm, "end": v(-15, -108) * mm});
            skLineSegment(sketch, "E88.MirrorCS", {"start": v(-15, -108) * mm, "end": v(-15, -120) * mm});
            skArc(sketch, "E89.MirrorCS", {"start": v(15, -120) * mm, "mid": v(0, -135) * mm, "end": v(-15, -120) * mm});
            skLineSegment(sketch, "E90.MirrorCS", {"start": v(15, -120) * mm, "end": v(15, -108) * mm});
            skLineSegment(sketch, "E91.MirrorCS", {"start": v(15, -108) * mm, "end": v(33, -90) * mm});
            skLineSegment(sketch, "E92.MirrorCS", {"start": v(0, -90) * mm, "end": v(0, -120) * mm, "construction": true});
            skCircle(sketch, "E93.MirrorC", {"center": v(0, -120) * mm, "radius": 6 * mm});
            skSolve(sketch);
        }
        {
            var Q0;
            {var subQ0=sQuery(id+"F16.wireOp",EDGE,"E87.MirrorCS");Q0=makeQuery(id+"F16.imprint","IMPRINT",FACE,{"disambiguationData":[TD([[makeQuery(id+"F16.imprint","IMPRINT",EDGE,{"derivedFrom":subQ0}),1.0]])]});}
            var Q1;
            Q1=makeQuery(id+"F16.imprint","IMPRINT",FACE,{"disambiguationData":[TD([[makeQuery(id+"F16.imprint","IMPRINT",EDGE,{"derivedFrom":sQuery(id+"F16.wireOp",EDGE,"E80")}),-1.0]])]});
            var Q2;
            Q2=makeQuery(id+"F16.imprint","IMPRINT",FACE,{"disambiguationData":[TD([[makeQuery(id+"F16.imprint","IMPRINT",EDGE,{"derivedFrom":makeQuery(id+"F1.opExtrude","CAP_EDGE",EDGE,{"disambiguationData":[OSD([sQuery(id+"F0.wireOp",EDGE,"E1.left")])],"isStart":true})}),-1.0]])]});
            var Q3;
            Q3=makeQuery(id+"F2.opExtrude","CAP_FACE",FACE,{"disambiguationData":[OSD([sQuery(id+"F0.wireOp",EDGE,"E12"),sQuery(id+"F0.wireOp",EDGE,"E13"),sQuery(id+"F0.wireOp",EDGE,"E14"),sQuery(id+"F0.wireOp",EDGE,"E15"),sQuery(id+"F0.wireOp",EDGE,"E17.filletArc"),sQuery(id+"F0.wireOp",EDGE,"E18.filletArc"),sQuery(id+"F0.wireOp",EDGE,"E19.filletArc"),sQuery(id+"F0.wireOp",EDGE,"E20.filletArc"),sQuery(id+"F0.wireOp",EDGE,"E25.0"),sQuery(id+"F0.wireOp",EDGE,"E25.1"),sQuery(id+"F0.wireOp",EDGE,"E25.2"),sQuery(id+"F0.wireOp",EDGE,"E25.3"),sQuery(id+"F0.wireOp",EDGE,"E25.4"),sQuery(id+"F0.wireOp",EDGE,"E25.5"),sQuery(id+"F0.wireOp",EDGE,"E25.6"),sQuery(id+"F0.wireOp",EDGE,"E25.7")])],"isStart":false});
            extrude(context, id + "F17", {"entities" : qUnion([Q0, Q1, Q2]), "operationType" : NewBodyOperationType.ADD, "endBound" : BoundingType.UP_TO_SURFACE, "endBoundEntityFace" : qUnion([Q3]), "depth" : 25 * mm});
        }
    });
